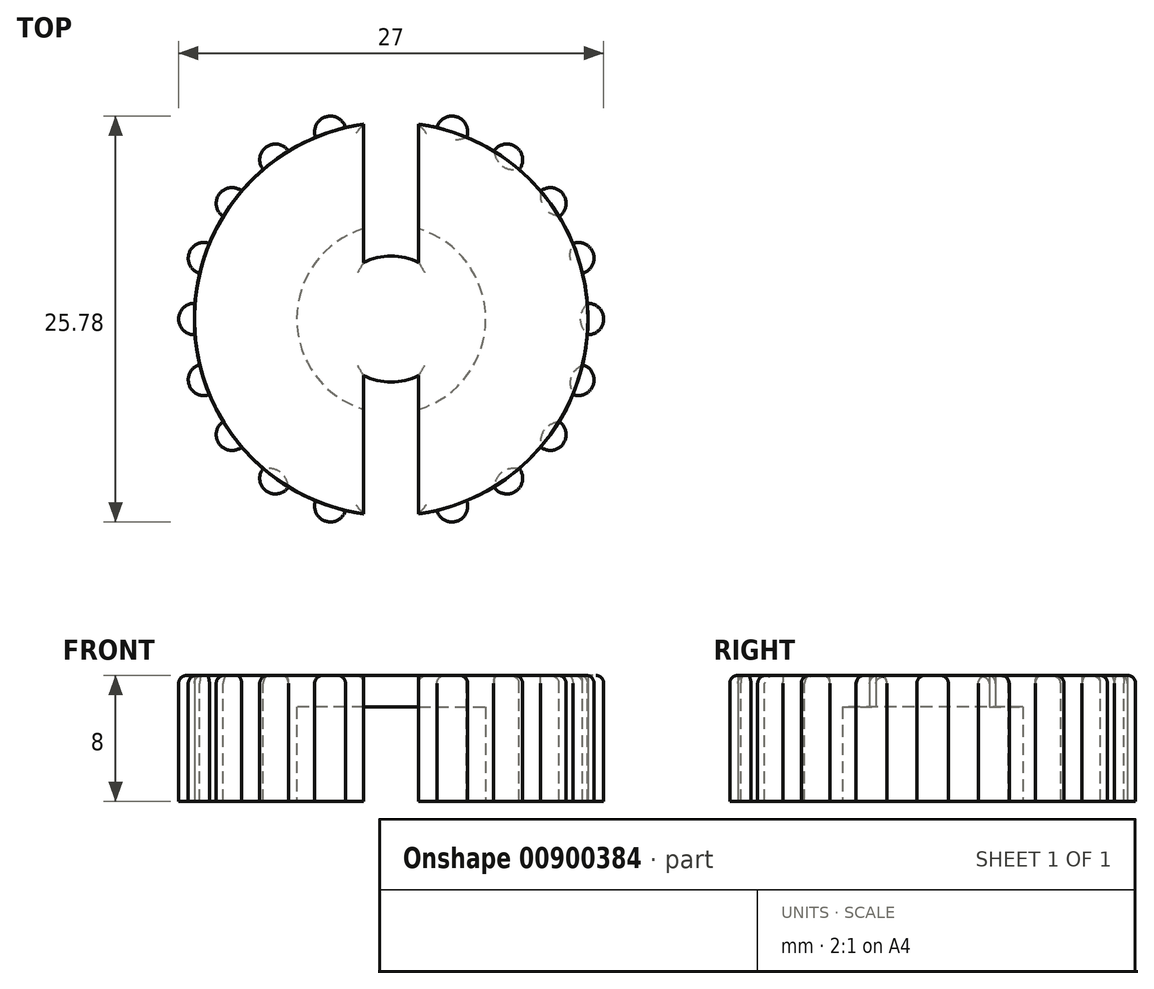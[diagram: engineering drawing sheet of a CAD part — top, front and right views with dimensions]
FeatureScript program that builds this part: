
annotation { "Feature Type Name" : "Feature", "Feature Type Description" : "" }
export const myFeature = defineFeature(function(context is Context, id is Id, definition is map)
    precondition{}
    {
        {
            var Q0;
            Q0=qCreatedBy(makeId("Top.planeOp"),FACE);
            var sketch = newSketch(context, id + "F0", { "sketchPlane" : qUnion([Q0])});
            skCircle(sketch, "E0", {"center": v(0, 0) * mm, "radius": 12.5 * mm});
            skCircle(sketch, "E1", {"center": v(0, 0) * mm, "radius": 6 * mm});
            skSolve(sketch);
        }
        {
            var Q0;
            Q0=makeQuery(id+"F0.imprint","IMPRINT",FACE,{"disambiguationData":[TD([[makeQuery(id+"F0.imprint","IMPRINT",EDGE,{"derivedFrom":sQuery(id+"F0.wireOp",EDGE,"E0")}),1.0]])]});
            var Q1;
            Q1=makeQuery(id+"F0.imprint","IMPRINT",FACE,{"disambiguationData":[TD([[makeQuery(id+"F0.imprint","IMPRINT",EDGE,{"derivedFrom":sQuery(id+"F0.wireOp",EDGE,"E1")}),1.0]])]});
            extrude(context, id + "F1", {"entities" : qUnion([Q0, Q1]), "depth" : 8 * mm, "offsetDistance" : 25 * mm});
        }
        {
            var Q0;
            Q0=makeQuery(id+"F1.opExtrude","CAP_FACE",FACE,{"disambiguationData":[OSD([sQuery(id+"F0.wireOp",EDGE,"E0")])],"isStart":false});
            var sketch = newSketch(context, id + "F2", { "sketchPlane" : qUnion([Q0])});
            skCircle(sketch, "E2", {"center": v(12.5, 0) * mm, "radius": 1 * mm});
            skSolve(sketch);
        }
        {
            var Q0;
            {var subQ0=sQuery(id+"F2.wireOp",EDGE,"E2");var subQ1=makeQuery(id+"F1.opExtrude","CAP_EDGE",EDGE,{"disambiguationData":[OSD([sQuery(id+"F0.wireOp",EDGE,"E0")])],"isStart":false});var subQ2=makeQuery(id+"F2.imprint","INTERSECT",VERTEX,{"disambiguationData":[OD(0.0)],"derivedFrom":[subQ1,subQ0]});Q0=makeQuery(id+"F2.imprint","IMPRINT",FACE,{"disambiguationData":[TD([[makeQuery(id+"F2.imprint","IMPRINT",EDGE,{"disambiguationData":[TD([[subQ2,-1.0]])],"derivedFrom":subQ0}),1.0]])]});}
            extrude(context, id + "F3", {"entities" : qUnion([Q0]), "operationType" : NewBodyOperationType.ADD, "oppositeDirection" : true, "depth" : 8 * mm, "offsetDistance" : 25 * mm});
        }
        {
            var Q0;
            Q0=qCreatedBy(makeId("Right.planeOp"),FACE);
            var sketch = newSketch(context, id + "F4", { "sketchPlane" : qUnion([Q0])});
            skLineSegment(sketch, "E3", {"start": v(0, 0) * mm, "end": v(0, 11.06) * mm});
            skSolve(sketch);
        }
        {
            var Q0;
            Q0=makeQuery(id+"F1.opExtrude","SWEPT_BODY",BODY,{"disambiguationData":[OSD([sQuery(id+"F0.wireOp",EDGE,"E0")])]});
            var Q1;
            Q1=sQuery(id+"F4.wireOp",EDGE,"E3");
            circularPattern(context, id + "F5", {"entities" : qUnion([Q0]), "axis" : qUnion([Q1]), "angle" : 360 * degree, "instanceCount" : 20, "equalSpace" : true});
        }
        {
            var Q0;
            Q0=makeQuery(id+"F0.imprint","IMPRINT",FACE,{"disambiguationData":[TD([[makeQuery(id+"F0.imprint","IMPRINT",EDGE,{"derivedFrom":sQuery(id+"F0.wireOp",EDGE,"E0")}),1.0]])]});
            var sketch = newSketch(context, id + "F6", { "sketchPlane" : qUnion([Q0])});
            skLineSegment(sketch, "E4", {"start": v(0, -15.16) * mm, "end": v(0, 16.37) * mm, "construction": true});
            skLineSegment(sketch, "E5", {"start": v(1.75, -12.38) * mm, "end": v(1.75, -5.74) * mm});
            skLineSegment(sketch, "E6", {"start": v(-1.75, -12.38) * mm, "end": v(-1.75, -5.74) * mm});
            skLineSegment(sketch, "E7", {"start": v(1.75, 5.74) * mm, "end": v(1.75, 12.38) * mm});
            skLineSegment(sketch, "E8", {"start": v(-1.75, 5.74) * mm, "end": v(-1.75, 12.38) * mm});
            skLineSegment(sketch, "E9", {"start": v(-1.75, -12.38) * mm, "end": v(-1.75, -14.26) * mm});
            skLineSegment(sketch, "E10", {"start": v(-1.75, -14.26) * mm, "end": v(1.77, -14.26) * mm});
            skLineSegment(sketch, "E11", {"start": v(1.77, -14.26) * mm, "end": v(1.75, -12.38) * mm});
            skLineSegment(sketch, "E12", {"start": v(-1.75, 12.38) * mm, "end": v(-1.75, 14.68) * mm});
            skLineSegment(sketch, "E13", {"start": v(-1.75, 14.68) * mm, "end": v(1.75, 14.68) * mm});
            skLineSegment(sketch, "E14", {"start": v(1.75, 14.68) * mm, "end": v(1.75, 12.38) * mm});
            skArc(sketch, "E15", {"start": v(-1.75, -3.6) * mm, "mid": v(0, -4) * mm, "end": v(1.75, -3.6) * mm});
            skLineSegment(sketch, "E16", {"start": v(-1.75, -5.74) * mm, "end": v(-1.75, -3.6) * mm});
            skLineSegment(sketch, "E17", {"start": v(1.75, -5.74) * mm, "end": v(1.75, -3.6) * mm});
            skLineSegment(sketch, "E18", {"start": v(-1.75, 5.74) * mm, "end": v(-1.75, 3.6) * mm});
            skLineSegment(sketch, "E19", {"start": v(1.75, 5.74) * mm, "end": v(1.75, 3.6) * mm});
            skArc(sketch, "E20.trimOffspring", {"start": v(1.75, 3.6) * mm, "mid": v(0, 4) * mm, "end": v(-1.75, 3.6) * mm});
            skSolve(sketch);
        }
        {
            var Q0;
            {var subQ0=sQuery(id+"F6.wireOp",EDGE,"E5");Q0=makeQuery(id+"F6.imprint","IMPRINT",FACE,{"disambiguationData":[TD([[makeQuery(id+"F6.imprint","IMPRINT",EDGE,{"derivedFrom":subQ0}),1.0]])]});}
            var Q1;
            {var subQ0=sQuery(id+"F6.wireOp",EDGE,"E7");Q1=makeQuery(id+"F6.imprint","IMPRINT",FACE,{"disambiguationData":[TD([[makeQuery(id+"F6.imprint","IMPRINT",EDGE,{"derivedFrom":subQ0}),1.0]])]});}
            var Q2;
            {var subQ0=sQuery(id+"F6.wireOp",EDGE,"E9");Q2=makeQuery(id+"F6.imprint","IMPRINT",FACE,{"disambiguationData":[TD([[makeQuery(id+"F6.imprint","IMPRINT",EDGE,{"derivedFrom":subQ0}),1.0]])]});}
            var Q3;
            {var subQ0=sQuery(id+"F6.wireOp",EDGE,"E12");Q3=makeQuery(id+"F6.imprint","IMPRINT",FACE,{"disambiguationData":[TD([[makeQuery(id+"F6.imprint","IMPRINT",EDGE,{"derivedFrom":subQ0}),-1.0]])]});}
            var Q4;
            Q4=makeQuery(id+"F6.imprint","IMPRINT",FACE,{"disambiguationData":[TD([[makeQuery(id+"F6.imprint","IMPRINT",EDGE,{"derivedFrom":sQuery(id+"F6.wireOp",EDGE,"E15")}),-1.0]])]});
            var Q5;
            {var subQ0=sQuery(id+"F6.wireOp",EDGE,"E18");Q5=makeQuery(id+"F6.imprint","IMPRINT",FACE,{"disambiguationData":[TD([[makeQuery(id+"F6.imprint","IMPRINT",EDGE,{"derivedFrom":subQ0}),1.0]])]});}
            extrude(context, id + "F7", {"entities" : qUnion([Q0, Q1, Q2, Q3, Q4, Q5]), "operationType" : NewBodyOperationType.REMOVE, "depth" : 8 * mm, "offsetDistance" : 25 * mm});
        }
        {
            var Q0;
            Q0=makeQuery(id+"F0.imprint","IMPRINT",FACE,{"disambiguationData":[TD([[makeQuery(id+"F0.imprint","IMPRINT",EDGE,{"derivedFrom":sQuery(id+"F0.wireOp",EDGE,"E1")}),1.0]])]});
            extrude(context, id + "F8", {"entities" : qUnion([Q0]), "operationType" : NewBodyOperationType.REMOVE, "depth" : 6 * mm, "offsetDistance" : 25 * mm});
        }
        {
            var Q0;
            Q0=makeQuery(id+"F5.opPattern","COPY",BODY,{"derivedFrom":makeQuery(id+"F1.opExtrude","SWEPT_BODY",BODY,{"disambiguationData":[OSD([sQuery(id+"F0.wireOp",EDGE,"E0")])]}),"instanceName":"15"});
            deleteBodies(context, id + "F9", {"entities" : qUnion([Q0])});
        }
        {
            var Q0;
            Q0=makeQuery(id+"F5.opPattern","COPY",BODY,{"derivedFrom":makeQuery(id+"F1.opExtrude","SWEPT_BODY",BODY,{"disambiguationData":[OSD([sQuery(id+"F0.wireOp",EDGE,"E0")])]}),"instanceName":"5"});
            deleteBodies(context, id + "F10", {"entities" : qUnion([Q0])});
        }
        {
            var Q0;
            {var subQ0=sQuery(id+"F0.wireOp",EDGE,"E0");Q0=makeQuery(id+"F5.opPattern","COPY",FACE,{"derivedFrom":makeQuery(id+"F3.boolean.opBoolean","MERGE",FACE,{"derivedFrom":[makeQuery(id+"F1.opExtrude","CAP_FACE",FACE,{"disambiguationData":[OSD([subQ0])],"isStart":false}),makeQuery(id+"F3.opExtrude","CAP_FACE",FACE,{"disambiguationData":[OSD([subQ0,sQuery(id+"F2.wireOp",EDGE,"E2")])],"isStart":true})]}),"instanceName":"19"});}
            var Q1;
            {var subQ0=sQuery(id+"F0.wireOp",EDGE,"E0");Q1=makeQuery(id+"F5.opPattern","COPY",FACE,{"derivedFrom":makeQuery(id+"F3.boolean.opBoolean","MERGE",FACE,{"derivedFrom":[makeQuery(id+"F1.opExtrude","CAP_FACE",FACE,{"disambiguationData":[OSD([subQ0])],"isStart":false}),makeQuery(id+"F3.opExtrude","CAP_FACE",FACE,{"disambiguationData":[OSD([subQ0,sQuery(id+"F2.wireOp",EDGE,"E2")])],"isStart":true})]}),"instanceName":"18"});}
            var Q2;
            {var subQ0=sQuery(id+"F0.wireOp",EDGE,"E0");Q2=makeQuery(id+"F5.opPattern","COPY",FACE,{"derivedFrom":makeQuery(id+"F3.boolean.opBoolean","MERGE",FACE,{"derivedFrom":[makeQuery(id+"F1.opExtrude","CAP_FACE",FACE,{"disambiguationData":[OSD([subQ0])],"isStart":false}),makeQuery(id+"F3.opExtrude","CAP_FACE",FACE,{"disambiguationData":[OSD([subQ0,sQuery(id+"F2.wireOp",EDGE,"E2")])],"isStart":true})]}),"instanceName":"17"});}
            var Q3;
            {var subQ1=sQuery(id+"F0.wireOp",EDGE,"E0");Q3=makeQuery(id+"F7.boolean.opBoolean","SPLIT",EDGE,{"disambiguationData":[TD([makeQuery(id+"F7.opExtrude","SWEPT_FACE",FACE,{"disambiguationData":[OSD([sQuery(id+"F6.wireOp",EDGE,"E7"),sQuery(id+"F6.wireOp",EDGE,"E19")])]})])],"derivedFrom":makeQuery(id+"F5.opPattern","COPY",EDGE,{"derivedFrom":makeQuery(id+"F1.opExtrude","CAP_EDGE",EDGE,{"disambiguationData":[OSD([subQ1])],"isStart":false}),"instanceName":"18"})});}
            var Q4;
            {var subQ1=sQuery(id+"F0.wireOp",EDGE,"E0");Q4=makeQuery(id+"F7.boolean.opBoolean","SPLIT",EDGE,{"disambiguationData":[TD([makeQuery(id+"F7.opExtrude","SWEPT_FACE",FACE,{"disambiguationData":[OSD([sQuery(id+"F6.wireOp",EDGE,"E7"),sQuery(id+"F6.wireOp",EDGE,"E19")])]})])],"derivedFrom":makeQuery(id+"F5.opPattern","COPY",EDGE,{"derivedFrom":makeQuery(id+"F1.opExtrude","CAP_EDGE",EDGE,{"disambiguationData":[OSD([subQ1])],"isStart":false}),"instanceName":"1"})});}
            var Q5;
            {var subQ0=sQuery(id+"F0.wireOp",EDGE,"E0");Q5=makeQuery(id+"F5.opPattern","COPY",FACE,{"derivedFrom":makeQuery(id+"F3.boolean.opBoolean","MERGE",FACE,{"derivedFrom":[makeQuery(id+"F1.opExtrude","CAP_FACE",FACE,{"disambiguationData":[OSD([subQ0])],"isStart":false}),makeQuery(id+"F3.opExtrude","CAP_FACE",FACE,{"disambiguationData":[OSD([subQ0,sQuery(id+"F2.wireOp",EDGE,"E2")])],"isStart":true})]}),"instanceName":"3"});}
            var Q6;
            {var subQ1=sQuery(id+"F0.wireOp",EDGE,"E0");Q6=makeQuery(id+"F7.boolean.opBoolean","SPLIT",EDGE,{"disambiguationData":[TD([makeQuery(id+"F7.opExtrude","SWEPT_FACE",FACE,{"disambiguationData":[OSD([sQuery(id+"F6.wireOp",EDGE,"E5"),sQuery(id+"F6.wireOp",EDGE,"E17")])]})])],"derivedFrom":makeQuery(id+"F5.opPattern","COPY",EDGE,{"derivedFrom":makeQuery(id+"F1.opExtrude","CAP_EDGE",EDGE,{"disambiguationData":[OSD([subQ1])],"isStart":false}),"instanceName":"4"})});}
            var Q7;
            {var subQ1=sQuery(id+"F0.wireOp",EDGE,"E0");Q7=makeQuery(id+"F7.boolean.opBoolean","SPLIT",EDGE,{"disambiguationData":[TD([makeQuery(id+"F7.opExtrude","SWEPT_FACE",FACE,{"disambiguationData":[OSD([sQuery(id+"F6.wireOp",EDGE,"E5"),sQuery(id+"F6.wireOp",EDGE,"E17")])]})])],"derivedFrom":makeQuery(id+"F5.opPattern","COPY",EDGE,{"derivedFrom":makeQuery(id+"F1.opExtrude","CAP_EDGE",EDGE,{"disambiguationData":[OSD([subQ1])],"isStart":false}),"instanceName":"2"})});}
            var Q8;
            Q8=makeQuery(id+"F5.opPattern","COPY",EDGE,{"derivedFrom":makeQuery(id+"F3.opExtrude","CAP_EDGE",EDGE,{"disambiguationData":[OSD([sQuery(id+"F2.wireOp",EDGE,"E2")])],"isStart":true}),"instanceName":"2"});
            var Q9;
            {var subQ1=sQuery(id+"F0.wireOp",EDGE,"E0");Q9=makeQuery(id+"F7.boolean.opBoolean","SPLIT",EDGE,{"disambiguationData":[TD([makeQuery(id+"F7.opExtrude","SWEPT_FACE",FACE,{"disambiguationData":[OSD([sQuery(id+"F6.wireOp",EDGE,"E5"),sQuery(id+"F6.wireOp",EDGE,"E17")])]})])],"derivedFrom":makeQuery(id+"F5.opPattern","COPY",EDGE,{"derivedFrom":makeQuery(id+"F1.opExtrude","CAP_EDGE",EDGE,{"disambiguationData":[OSD([subQ1])],"isStart":false}),"instanceName":"3"})});}
            var Q10;
            Q10=makeQuery(id+"F5.opPattern","COPY",EDGE,{"derivedFrom":makeQuery(id+"F3.opExtrude","CAP_EDGE",EDGE,{"disambiguationData":[OSD([sQuery(id+"F2.wireOp",EDGE,"E2")])],"isStart":true}),"instanceName":"1"});
            var Q11;
            Q11=makeQuery(id+"F5.opPattern","COPY",EDGE,{"derivedFrom":makeQuery(id+"F3.opExtrude","CAP_EDGE",EDGE,{"disambiguationData":[OSD([sQuery(id+"F2.wireOp",EDGE,"E2")])],"isStart":true}),"instanceName":"4"});
            var Q12;
            Q12=makeQuery(id+"F5.opPattern","COPY",EDGE,{"derivedFrom":makeQuery(id+"F3.opExtrude","CAP_EDGE",EDGE,{"disambiguationData":[OSD([sQuery(id+"F2.wireOp",EDGE,"E2")])],"isStart":true}),"instanceName":"6"});
            var Q13;
            Q13=makeQuery(id+"F5.opPattern","COPY",EDGE,{"derivedFrom":makeQuery(id+"F3.opExtrude","CAP_EDGE",EDGE,{"disambiguationData":[OSD([sQuery(id+"F2.wireOp",EDGE,"E2")])],"isStart":true}),"instanceName":"7"});
            var Q14;
            Q14=makeQuery(id+"F5.opPattern","COPY",EDGE,{"derivedFrom":makeQuery(id+"F3.opExtrude","CAP_EDGE",EDGE,{"disambiguationData":[OSD([sQuery(id+"F2.wireOp",EDGE,"E2")])],"isStart":true}),"instanceName":"8"});
            var Q15;
            Q15=makeQuery(id+"F5.opPattern","COPY",EDGE,{"derivedFrom":makeQuery(id+"F3.opExtrude","CAP_EDGE",EDGE,{"disambiguationData":[OSD([sQuery(id+"F2.wireOp",EDGE,"E2")])],"isStart":true}),"instanceName":"9"});
            var Q16;
            Q16=makeQuery(id+"F5.opPattern","COPY",EDGE,{"derivedFrom":makeQuery(id+"F3.opExtrude","CAP_EDGE",EDGE,{"disambiguationData":[OSD([sQuery(id+"F2.wireOp",EDGE,"E2")])],"isStart":true}),"instanceName":"10"});
            var Q17;
            Q17=makeQuery(id+"F5.opPattern","COPY",EDGE,{"derivedFrom":makeQuery(id+"F3.opExtrude","CAP_EDGE",EDGE,{"disambiguationData":[OSD([sQuery(id+"F2.wireOp",EDGE,"E2")])],"isStart":true}),"instanceName":"11"});
            var Q18;
            Q18=makeQuery(id+"F5.opPattern","COPY",EDGE,{"derivedFrom":makeQuery(id+"F3.opExtrude","CAP_EDGE",EDGE,{"disambiguationData":[OSD([sQuery(id+"F2.wireOp",EDGE,"E2")])],"isStart":true}),"instanceName":"12"});
            var Q19;
            {var subQ0=sQuery(id+"F0.wireOp",EDGE,"E0");Q19=makeQuery(id+"F5.opPattern","COPY",FACE,{"derivedFrom":makeQuery(id+"F3.boolean.opBoolean","MERGE",FACE,{"derivedFrom":[makeQuery(id+"F1.opExtrude","CAP_FACE",FACE,{"disambiguationData":[OSD([subQ0])],"isStart":false}),makeQuery(id+"F3.opExtrude","CAP_FACE",FACE,{"disambiguationData":[OSD([subQ0,sQuery(id+"F2.wireOp",EDGE,"E2")])],"isStart":true})]}),"instanceName":"13"});}
            var Q20;
            Q20=makeQuery(id+"F5.opPattern","COPY",EDGE,{"derivedFrom":makeQuery(id+"F3.opExtrude","CAP_EDGE",EDGE,{"disambiguationData":[OSD([sQuery(id+"F2.wireOp",EDGE,"E2")])],"isStart":true}),"instanceName":"14"});
            var Q21;
            {var subQ0=sQuery(id+"F0.wireOp",EDGE,"E0");Q21=makeQuery(id+"F5.opPattern","COPY",FACE,{"derivedFrom":makeQuery(id+"F3.boolean.opBoolean","MERGE",FACE,{"derivedFrom":[makeQuery(id+"F1.opExtrude","CAP_FACE",FACE,{"disambiguationData":[OSD([subQ0])],"isStart":false}),makeQuery(id+"F3.opExtrude","CAP_FACE",FACE,{"disambiguationData":[OSD([subQ0,sQuery(id+"F2.wireOp",EDGE,"E2")])],"isStart":true})]}),"instanceName":"2"});}
            var Q22;
            Q22=makeQuery(id+"F5.opPattern","COPY",EDGE,{"derivedFrom":makeQuery(id+"F3.opExtrude","CAP_EDGE",EDGE,{"disambiguationData":[OSD([sQuery(id+"F2.wireOp",EDGE,"E2")])],"isStart":true}),"instanceName":"16"});
            var Q23;
            {var subQ0=sQuery(id+"F0.wireOp",EDGE,"E0");Q23=makeQuery(id+"F3.boolean.opBoolean","MERGE",FACE,{"derivedFrom":[makeQuery(id+"F1.opExtrude","CAP_FACE",FACE,{"disambiguationData":[OSD([subQ0])],"isStart":false}),makeQuery(id+"F3.opExtrude","CAP_FACE",FACE,{"disambiguationData":[OSD([subQ0,sQuery(id+"F2.wireOp",EDGE,"E2")])],"isStart":true})]});}
            fillet(context, id + "F11", {"entities" : qUnion([Q0, Q1, Q2, Q3, Q4, Q5, Q6, Q7, Q8, Q9, Q10, Q11, Q12, Q13, Q14, Q15, Q16, Q17, Q18, Q19, Q20, Q21, Q22, Q23]), "radius" : .5 * mm, "tangentPropagation" : true, "allowEdgeOverflow" : false});
        }
    });
